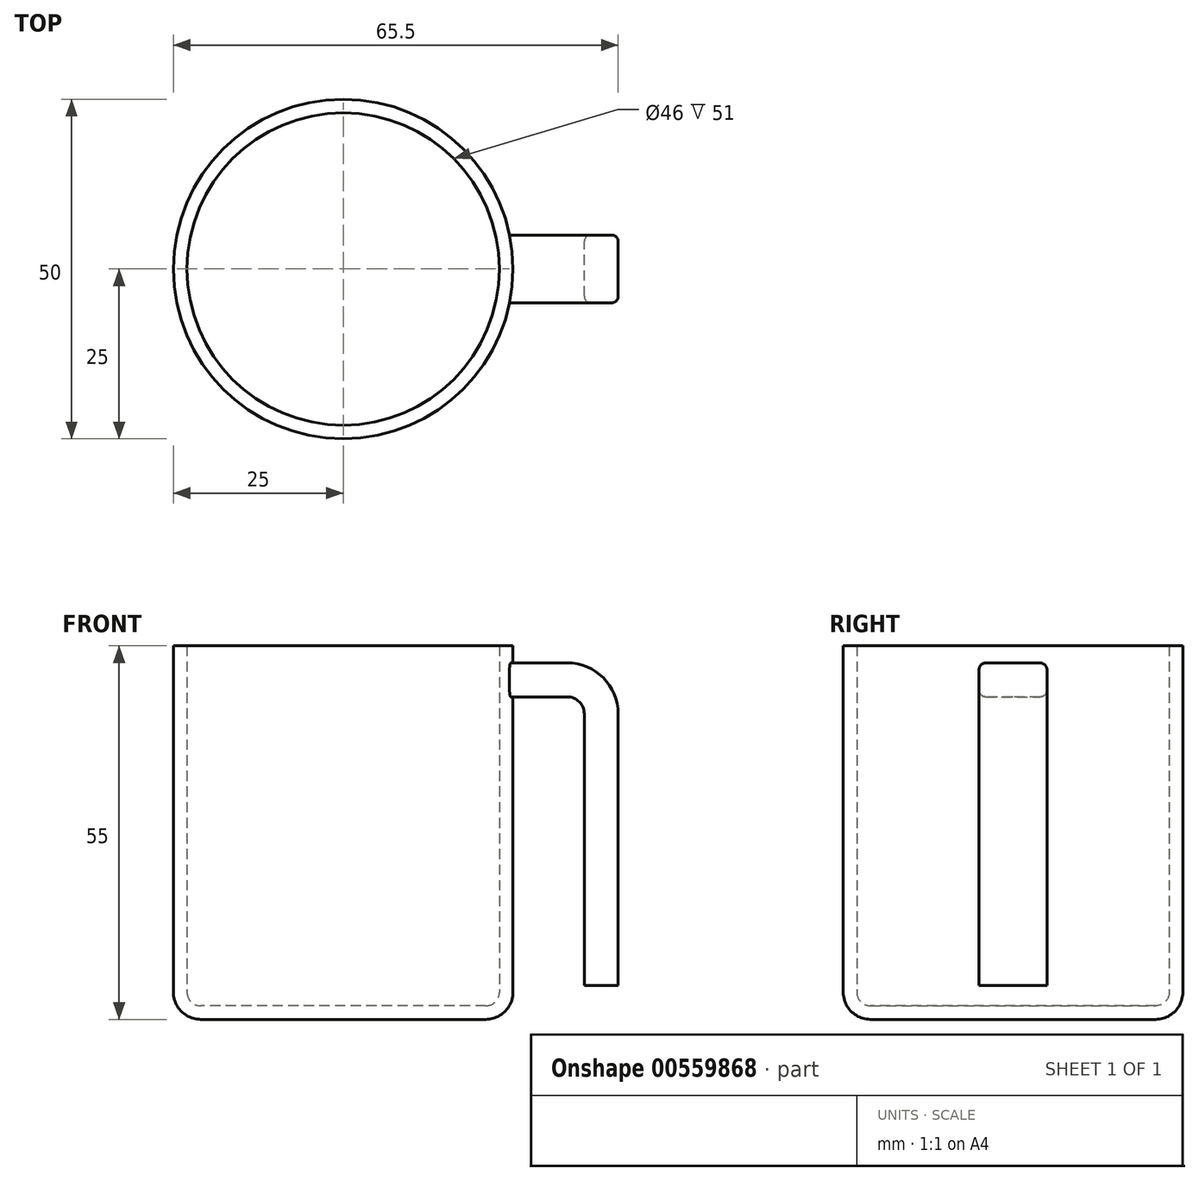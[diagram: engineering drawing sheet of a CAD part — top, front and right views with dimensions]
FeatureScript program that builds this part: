
annotation { "Feature Type Name" : "Feature", "Feature Type Description" : "" }
export const myFeature = defineFeature(function(context is Context, id is Id, definition is map)
    precondition{}
    {
        {
            var Q0;
            Q0=qCreatedBy(makeId("Top.planeOp"),FACE);
            var sketch = newSketch(context, id + "F0", { "sketchPlane" : qUnion([Q0])});
            skCircle(sketch, "E0", {"center": v(0, 0) * mm, "radius": 25 * mm});
            skSolve(sketch);
        }
        {
            var Q0;
            Q0 = qSketchRegion(id + "F0", true);
            extrude(context, id + "F1", {"entities" : qUnion([Q0]), "depth" : 55 * mm, "offsetDistance" : 25 * mm});
        }
        {
            var Q0;
            Q0=makeQuery(id+"F1.opExtrude","CAP_EDGE",EDGE,{"disambiguationData":[OSD([sQuery(id+"F0.wireOp",EDGE,"E0")])],"isStart":true});
            fillet(context, id + "F2", {"entities" : qUnion([Q0]), "radius" : 4 * mm, "tangentPropagation" : true, "allowEdgeOverflow" : false});
        }
        {
            var Q0;
            Q0=makeQuery(id+"F1.opExtrude","CAP_FACE",FACE,{"disambiguationData":[OSD([sQuery(id+"F0.wireOp",EDGE,"E0")])],"isStart":false});
            var sketch = newSketch(context, id + "F3", { "sketchPlane" : qUnion([Q0])});
            skCircle(sketch, "E1", {"center": v(0, 0) * mm, "radius": 23 * mm});
            skSolve(sketch);
        }
        {
            var Q0;
            Q0=qCreatedBy(makeId("Right.planeOp"),FACE);
            var sketch = newSketch(context, id + "F4", { "sketchPlane" : qUnion([Q0])});
            skLineSegment(sketch, "E2.bottom", {"start": v(-5, 52.5) * mm, "end": v(5, 52.5) * mm});
            skLineSegment(sketch, "E2.top", {"start": v(-5, 47.5) * mm, "end": v(5, 47.5) * mm});
            skLineSegment(sketch, "E2.left", {"start": v(-5, 52.5) * mm, "end": v(-5, 47.5) * mm});
            skLineSegment(sketch, "E2.right", {"start": v(5, 52.5) * mm, "end": v(5, 47.5) * mm});
            skSolve(sketch);
        }
        {
            var Q0;
            Q0=sQuery(id+"F4.wireOp",EDGE,"E2.left");
            cPoint(context, id + "F5", {"entities" : qUnion([Q0]), "parameter" : 0.5});
        }
        {
            var Q0;
            Q0=sQuery(id+"F4.wireOp",EDGE,"E2.top");
            cPoint(context, id + "F6", {"entities" : qUnion([Q0]), "parameter" : 0.5});
        }
        {
            var Q0;
            Q0=sQuery(id+"F4.wireOp",EDGE,"E2.right");
            cPoint(context, id + "F7", {"entities" : qUnion([Q0]), "parameter" : 0.5});
        }
        {
            var Q0;
            Q0 = qCreatedBy(id + "F5" ,VERTEX);
            var Q1;
            Q1 = qCreatedBy(id + "F6" ,VERTEX);
            var Q2;
            Q2 = qCreatedBy(id + "F7" ,VERTEX);
            cPlane(context, id + "F8", {"entities" : qUnion([Q0, Q1, Q2]), "cplaneType" : CPlaneType.THREE_POINT, "offset" : 25 * mm, "width" : 150 * mm, "height" : 150 * mm});
        }
        {
            var Q0;
            Q0=qCreatedBy(id+"F8.planeOp",FACE);
            var sketch = newSketch(context, id + "F9", { "sketchPlane" : qUnion([Q0])});
            skLineSegment(sketch, "E3", {"start": v(-5, 52.5) * mm, "end": v(5, 47.5) * mm});
            skSolve(sketch);
        }
        {
            var Q0;
            Q0=qCreatedBy(id+"F8.planeOp",FACE);
            var sketch = newSketch(context, id + "F10", { "sketchPlane" : qUnion([Q0])});
            skLineSegment(sketch, "E4", {"start": v(-5, 47.5) * mm, "end": v(5, 52.5) * mm});
            skSolve(sketch);
        }
        {
            var Q0;
            Q0=sQuery(id+"F10.wireOp",EDGE,"E4");
            cPoint(context, id + "F11", {"entities" : qUnion([Q0]), "parameter" : 0.5});
        }
        {
            var Q0;
            Q0 = qCreatedBy(id + "F11" ,VERTEX);
            var Q1;
            Q1=qCreatedBy(makeId("Front.planeOp"),FACE);
            cPlane(context, id + "F12", {"entities" : qUnion([Q0, Q1]), "cplaneType" : CPlaneType.PLANE_POINT, "offset" : 25 * mm, "width" : 150 * mm, "height" : 150 * mm});
        }
        {
            var Q0;
            Q0=qCreatedBy(id+"F12.planeOp",FACE);
            var sketch = newSketch(context, id + "F13", { "sketchPlane" : qUnion([Q0])});
            skLineSegment(sketch, "E5", {"start": v(0, 50) * mm, "end": v(33, 50) * mm});
            skLineSegment(sketch, "E6", {"start": v(38, 45) * mm, "end": v(38, 5) * mm});
            skPoint(sketch, "E7.visualSharp", {"position": v(38, 50) * mm});
            skArc(sketch, "E7.filletArc", {"start": v(38, 45) * mm, "mid": v(36.54, 48.54) * mm, "end": v(33, 50) * mm});
            skSolve(sketch);
        }
        {
            var Q0;
            Q0=makeQuery(id+"F1.opExtrude","CAP_FACE",FACE,{"disambiguationData":[OSD([sQuery(id+"F0.wireOp",EDGE,"E0")])],"isStart":false});
            shell(context, id + "F14", {"entities" : qUnion([Q0]), "thickness" : 2 * mm});
        }
        {
            var Q0;
            Q0=makeQuery(id+"F4.imprint","IMPRINT",FACE,{"disambiguationData":[TD([[makeQuery(id+"F4.imprint","IMPRINT",EDGE,{"derivedFrom":sQuery(id+"F4.wireOp",EDGE,"E2.bottom")}),-1.0]])]});
            var Q1;
            Q1 = qConstructionFilter(qBodyType(qCreatedBy(id + "F13" ,EDGE), BodyType.WIRE), ConstructionObject.NO);
            sweep(context, id + "F15", {"operationType" : NewBodyOperationType.ADD, "profiles" : qUnion([Q0]), "path" : qUnion([Q1])});
        }
        {
            var Q0;
            Q0=makeQuery(id+"F15.opSweep","SWEPT_EDGE",EDGE,{"disambiguationData":[OSD([sQuery(id+"F4.wireOp",EDGE,"E2.bottom"),sQuery(id+"F4.wireOp",EDGE,"E2.left"),sQuery(id+"F13.wireOp",EDGE,"E6")])]});
            var Q1;
            Q1=makeQuery(id+"F15.opSweep","SWEPT_EDGE",EDGE,{"disambiguationData":[OSD([sQuery(id+"F4.wireOp",EDGE,"E2.bottom"),sQuery(id+"F4.wireOp",EDGE,"E2.right"),sQuery(id+"F13.wireOp",EDGE,"E6")])]});
            var Q2;
            Q2=makeQuery(id+"F15.opSweep","SWEPT_EDGE",EDGE,{"disambiguationData":[OSD([sQuery(id+"F4.wireOp",EDGE,"E2.top"),sQuery(id+"F4.wireOp",EDGE,"E2.left"),sQuery(id+"F13.wireOp",EDGE,"E6")])]});
            var Q3;
            Q3=makeQuery(id+"F15.opSweep","SWEPT_EDGE",EDGE,{"disambiguationData":[OSD([sQuery(id+"F4.wireOp",EDGE,"E2.top"),sQuery(id+"F4.wireOp",EDGE,"E2.right"),sQuery(id+"F13.wireOp",EDGE,"E6")])]});
            fillet(context, id + "F16", {"entities" : qUnion([Q0, Q1, Q2, Q3]), "radius" : 1 * mm, "tangentPropagation" : true, "allowEdgeOverflow" : false});
        }
        {
            var Q0;
            Q0=makeQuery(id+"F3.imprint","IMPRINT",FACE,{"disambiguationData":[TD([[makeQuery(id+"F3.imprint","IMPRINT",EDGE,{"derivedFrom":sQuery(id+"F3.wireOp",EDGE,"E1")}),1.0]])]});
            extrude(context, id + "F17", {"entities" : qUnion([Q0]), "operationType" : NewBodyOperationType.REMOVE, "oppositeDirection" : true, "depth" : 50 * mm, "offsetDistance" : 25 * mm});
        }
    });
